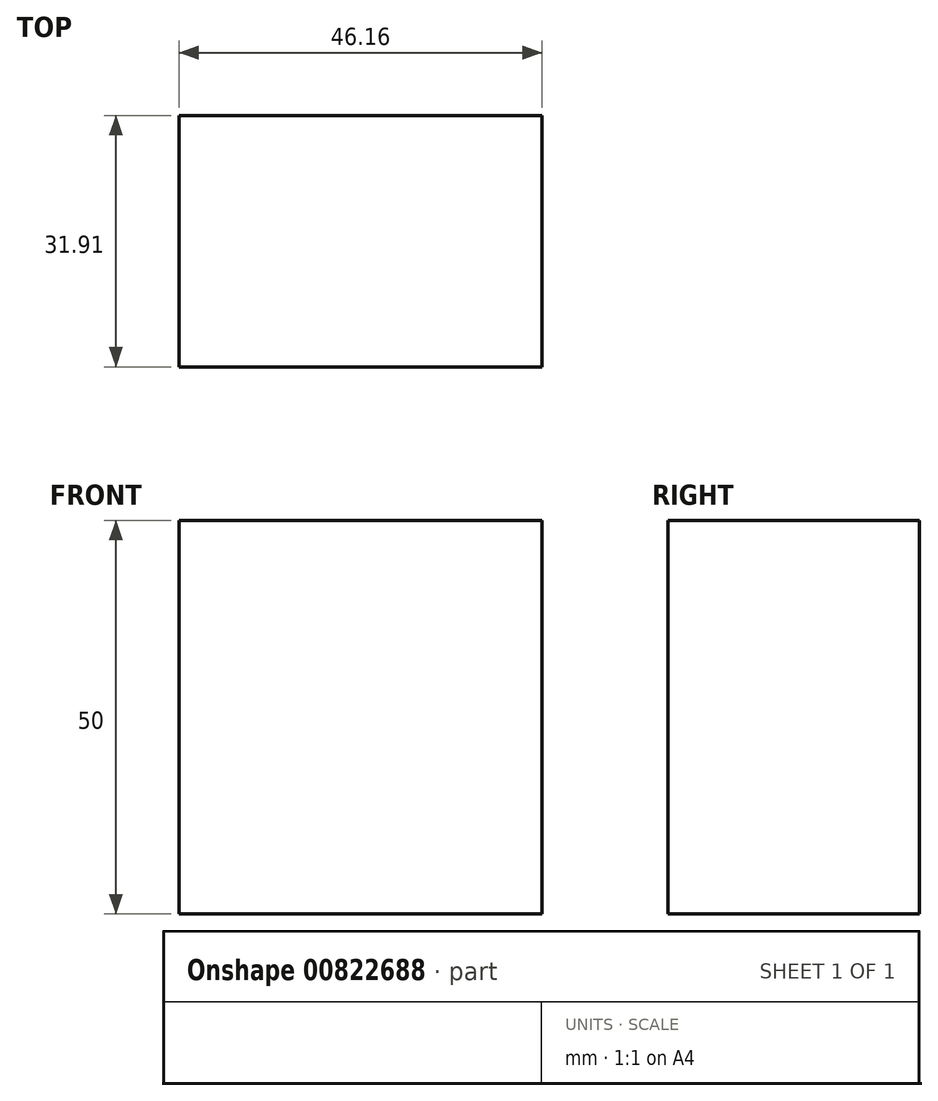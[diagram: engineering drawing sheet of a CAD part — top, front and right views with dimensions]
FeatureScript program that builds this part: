
annotation { "Feature Type Name" : "Feature", "Feature Type Description" : "" }
export const myFeature = defineFeature(function(context is Context, id is Id, definition is map)
    precondition{}
    {
        {
            var Q0;
            Q0=qCreatedBy(makeId("Top.planeOp"),FACE);
            var sketch = newSketch(context, id + "F0", { "sketchPlane" : qUnion([Q0])});
            skLineSegment(sketch, "E0.bottom", {"start": v(-22.75, -38.23) * mm, "end": v(23.41, -38.23) * mm});
            skLineSegment(sketch, "E0.top", {"start": v(-22.75, -6.32) * mm, "end": v(23.41, -6.32) * mm});
            skLineSegment(sketch, "E0.left", {"start": v(-22.75, -38.23) * mm, "end": v(-22.75, -6.32) * mm});
            skLineSegment(sketch, "E0.right", {"start": v(23.41, -38.23) * mm, "end": v(23.41, -6.32) * mm});
            skSolve(sketch);
        }
        {
            var Q0;
            Q0=makeQuery(id+"F0.imprint","IMPRINT",FACE,{"disambiguationData":[TD([[makeQuery(id+"F0.imprint","IMPRINT",EDGE,{"derivedFrom":sQuery(id+"F0.wireOp",EDGE,"E0.bottom")}),1.0]])]});
            extrude(context, id + "F1", {"entities" : qUnion([Q0]), "depth" : 50 * mm, "offsetDistance" : 25 * mm});
        }
    });
